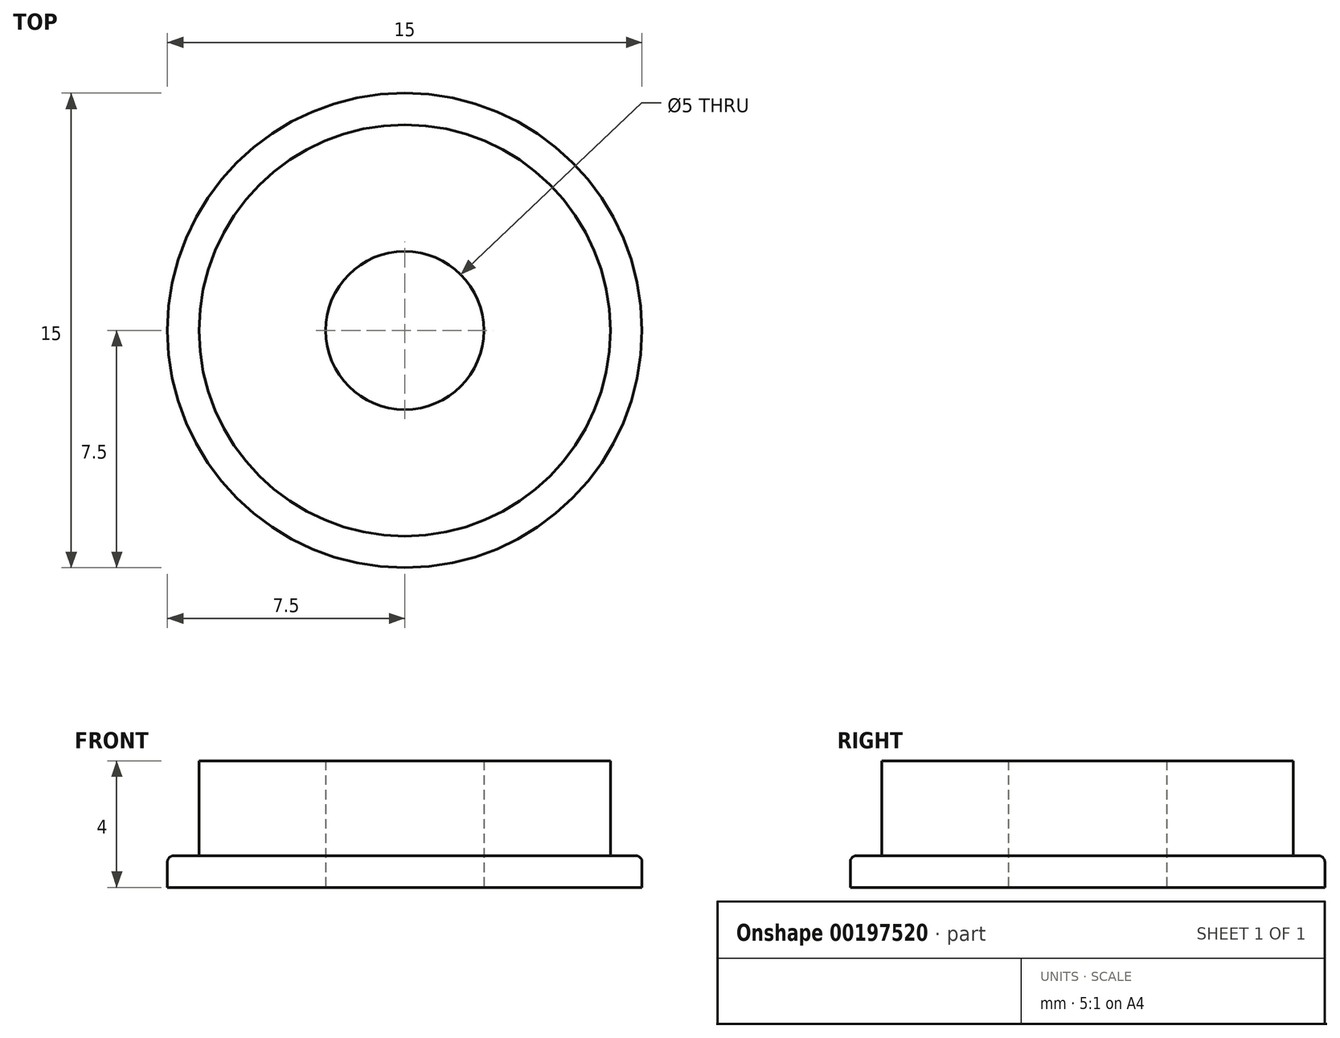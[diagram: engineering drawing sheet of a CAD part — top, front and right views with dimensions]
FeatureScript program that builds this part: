
annotation { "Feature Type Name" : "Feature", "Feature Type Description" : "" }
export const myFeature = defineFeature(function(context is Context, id is Id, definition is map)
    precondition{}
    {
        {
            var Q0;
            Q0=qCreatedBy(makeId("Top.planeOp"),FACE);
            var sketch = newSketch(context, id + "F0", { "sketchPlane" : qUnion([Q0])});
            skCircle(sketch, "E0", {"center": v(0, 0) * mm, "radius": 2.5 * mm});
            skCircle(sketch, "E1", {"center": v(0, 0) * mm, "radius": 7.5 * mm});
            skSolve(sketch);
        }
        {
            var Q0;
            Q0=qSketchRegion(id+"F0",true);
            extrude(context, id + "F1", {"entities" : qUnion([Q0]), "depth" : 1 * mm});
        }
        {
            var Q0;
            Q0=makeQuery(id+"F1.opExtrude","CAP_FACE",FACE,{"disambiguationData":[OSD([sQuery(id+"F0.wireOp",EDGE,"E0"),sQuery(id+"F0.wireOp",EDGE,"E1")])],"isStart":false});
            var sketch = newSketch(context, id + "F2", { "sketchPlane" : qUnion([Q0])});
            skCircle(sketch, "E2.0", {"center": v(0, 0) * mm, "radius": 2.5 * mm});
            skCircle(sketch, "E3", {"center": v(0, 0) * mm, "radius": 6.5 * mm});
            skSolve(sketch);
        }
        {
            var Q0;
            Q0=qSketchRegion(id+"F2",true);
            extrude(context, id + "F3", {"entities" : qUnion([Q0]), "operationType" : NewBodyOperationType.ADD, "depth" : 3 * mm});
        }
        {
            var Q0;
            Q0=makeQuery(id+"F1.opExtrude","CAP_EDGE",EDGE,{"disambiguationData":[OSD([sQuery(id+"F0.wireOp",EDGE,"E1")])],"isStart":false});
            fillet(context, id + "F4", {"entities" : qUnion([Q0]), "radius" : .2 * mm, "tangentPropagation" : true, "allowEdgeOverflow" : false});
        }
    });
